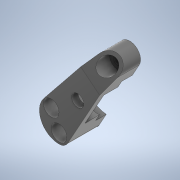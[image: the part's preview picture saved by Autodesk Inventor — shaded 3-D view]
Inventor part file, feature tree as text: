
AUTODESK INVENTOR PART (.ipt)
format: ipt  version: 2020 (Build 240168000, 168)  size: 219,648 bytes
history: native  units: mm
features: extrude x5, sketch x5
ambient origin geometry x8: Origin, YZ Plane, XZ Plane, XY Plane, X Axis, Y Axis, Z Axis, Center Point
bodies: Solid1 (feature_tree)
feature tree (10):
  extrude  "Extrusion1"  Depth=24.0mm
  extrude  "Extrusion2"  Depth=3.0mm
  extrude  "Extrusion3"  Depth=2.1mm
  extrude  "Extrusion4"  Depth=2.5mm
  extrude  "Extrusion5"  Depth=10.0mm
  sketch  "Sketch1"  dims[d0=18.0mm d1=24.0mm]
  sketch  "Sketch3"  dims[d2=2.1mm d3=3.0mm]
  sketch  "Sketch5"  dims[d4=3.0mm d5=2.1mm]
  sketch  "Sketch6"  dims[d6=2.1mm d7=2.5mm]
  sketch  "Sketch8"  dims[d8=5.0mm d9=3.0mm d10=7.0mm d12=10.0mm d15=6.0mm d16=8.0mm d17=0.0mm d18=3.1mm d25=5.5mm d26=10.0mm d27=14.9mm d28=2.7mm d29=0.0mm d30=12.0mm d31=8.251mm d32=4.0mm d33=4.0mm d34=4.0mm d35=4.9mm d36=0.0mm d37=11.4mm d38=3.65mm d39=0.0mm d40=10.0mm d41=0.0mm]
